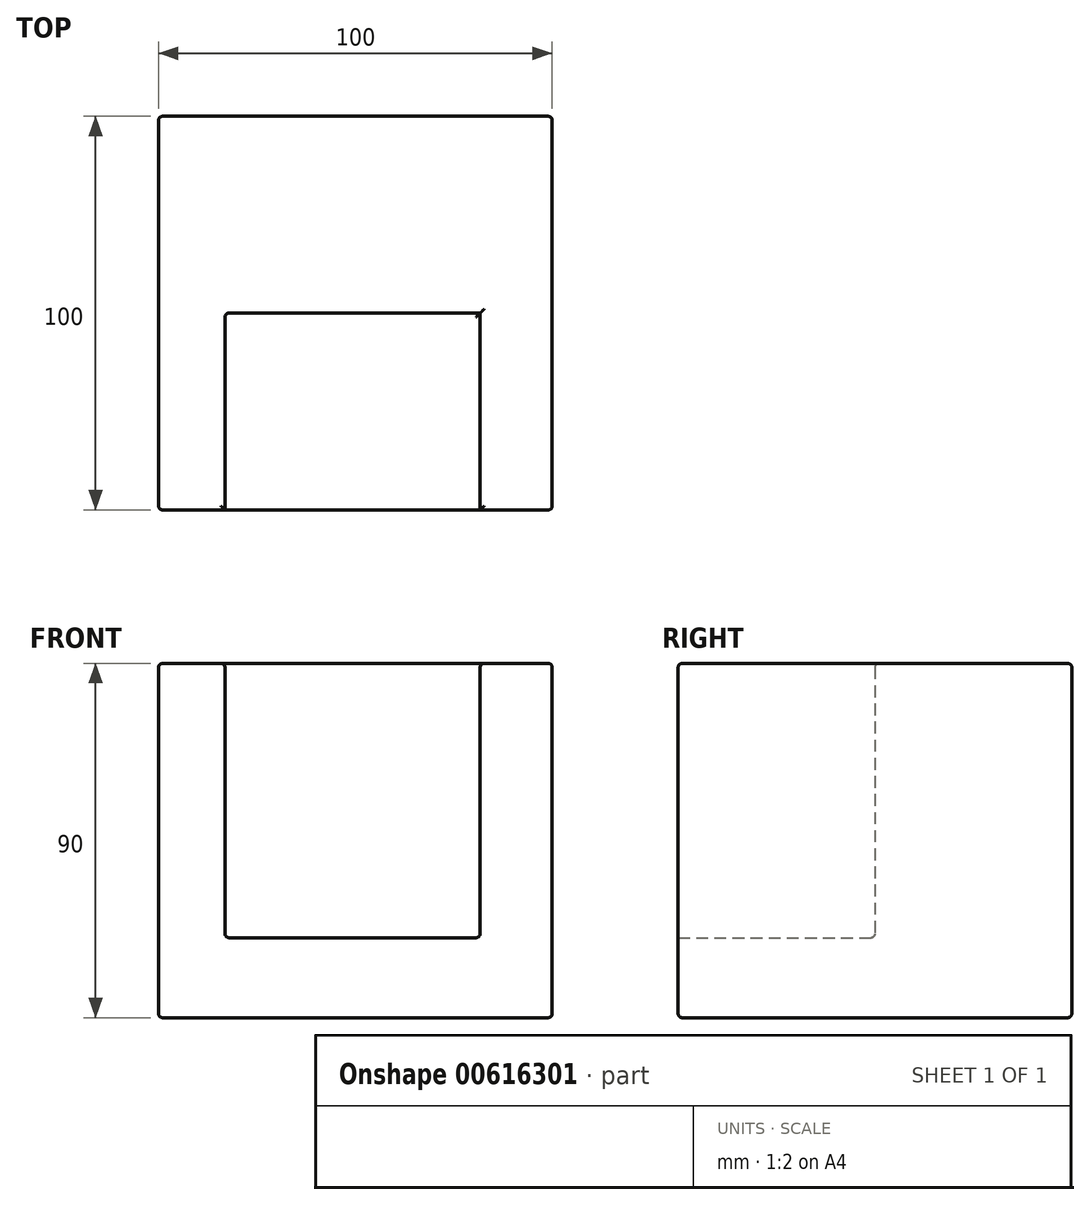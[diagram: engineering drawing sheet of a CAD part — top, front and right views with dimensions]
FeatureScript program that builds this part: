
annotation { "Feature Type Name" : "Feature", "Feature Type Description" : "" }
export const myFeature = defineFeature(function(context is Context, id is Id, definition is map)
    precondition{}
    {
        {
            var Q0;
            Q0=qCreatedBy(makeId("Top.planeOp"),FACE);
            var sketch = newSketch(context, id + "F0", { "sketchPlane" : qUnion([Q0])});
            skLineSegment(sketch, "E0.bottom", {"start": v(50, -50) * mm, "end": v(-50, -50) * mm});
            skLineSegment(sketch, "E0.top", {"start": v(50, 50) * mm, "end": v(-50, 50) * mm});
            skLineSegment(sketch, "E0.left", {"start": v(50, -50) * mm, "end": v(50, 50) * mm});
            skLineSegment(sketch, "E0.right", {"start": v(-50, -50) * mm, "end": v(-50, 50) * mm});
            skPoint(sketch, "E0.middle", {"position": v(0, 0) * mm});
            skSolve(sketch);
        }
        {
            var Q0;
            Q0 = qSketchRegion(id + "F0", true);
            extrude(context, id + "F1", {"entities" : qUnion([Q0]), "depth" : 90 * mm, "offsetDistance" : 25 * mm});
        }
        {
            var Q0;
            Q0=qCreatedBy(makeId("Front.planeOp"),FACE);
            var sketch = newSketch(context, id + "F2", { "sketchPlane" : qUnion([Q0])});
            skLineSegment(sketch, "E1.bottom", {"start": v(-33.14, 90.96) * mm, "end": v(31.7, 90.96) * mm});
            skLineSegment(sketch, "E1.top", {"start": v(-33.14, 20.32) * mm, "end": v(31.7, 20.32) * mm});
            skLineSegment(sketch, "E1.left", {"start": v(-33.14, 90.96) * mm, "end": v(-33.14, 20.32) * mm});
            skLineSegment(sketch, "E1.right", {"start": v(31.7, 90.96) * mm, "end": v(31.7, 20.32) * mm});
            skSolve(sketch);
        }
        {
            var Q0;
            Q0 = qSketchRegion(id + "F2", true);
            extrude(context, id + "F3", {"entities" : qUnion([Q0]), "operationType" : NewBodyOperationType.REMOVE, "depth" : 50 * mm, "offsetDistance" : 25 * mm});
        }
        {
            var Q0;
            Q0=qCreatedBy(makeId("Top.planeOp"),FACE);
            var sketch = newSketch(context, id + "F4", { "sketchPlane" : qUnion([Q0])});
            skLineSegment(sketch, "E2.bottom", {"start": v(-32.9, 0) * mm, "end": v(32.4, 0) * mm});
            skLineSegment(sketch, "E2.top", {"start": v(-32.9, 31.19) * mm, "end": v(32.4, 31.19) * mm});
            skLineSegment(sketch, "E2.left", {"start": v(-32.9, 0) * mm, "end": v(-32.9, 31.19) * mm});
            skLineSegment(sketch, "E2.right", {"start": v(32.4, 0) * mm, "end": v(32.4, 31.19) * mm});
            skSolve(sketch);
        }
        {
            var Q0;
            Q0 = qSketchRegion(id + "F4", true);
            extrude(context, id + "F5", {"entities" : qUnion([Q0]), "operationType" : NewBodyOperationType.ADD, "depth" : 25 * mm, "offsetDistance" : 25 * mm});
        }
        {
            var Q0;
            Q0 = qSketchRegion(id + "F4", true);
            extrude(context, id + "F6", {"entities" : qUnion([Q0]), "operationType" : NewBodyOperationType.ADD, "depth" : 50 * mm, "offsetDistance" : 25 * mm});
        }
        {
            var Q0;
            Q0=makeQuery(id+"F3.boolean.opBoolean","INTERSECT",EDGE,{"derivedFrom":[makeQuery(id+"F1.opExtrude","CAP_FACE",FACE,{"disambiguationData":[OSD([sQuery(id+"F0.wireOp",EDGE,"E0.bottom"),sQuery(id+"F0.wireOp",EDGE,"E0.top"),sQuery(id+"F0.wireOp",EDGE,"E0.left"),sQuery(id+"F0.wireOp",EDGE,"E0.right")])],"isStart":false}),makeQuery(id+"F3.opExtrude","CAP_FACE",FACE,{"disambiguationData":[OSD([sQuery(id+"F2.wireOp",EDGE,"E1.bottom"),sQuery(id+"F2.wireOp",EDGE,"E1.top"),sQuery(id+"F2.wireOp",EDGE,"E1.left"),sQuery(id+"F2.wireOp",EDGE,"E1.right")])],"isStart":true})]});
            fillet(context, id + "F7", {"entities" : qUnion([Q0]), "radius" : 1 * mm, "tangentPropagation" : true, "allowEdgeOverflow" : false});
        }
        {
            var Q0;
            Q0=makeQuery(id+"F3.boolean.opBoolean","INTERSECT",EDGE,{"derivedFrom":[makeQuery(id+"F1.opExtrude","CAP_FACE",FACE,{"disambiguationData":[OSD([sQuery(id+"F0.wireOp",EDGE,"E0.bottom"),sQuery(id+"F0.wireOp",EDGE,"E0.top"),sQuery(id+"F0.wireOp",EDGE,"E0.left"),sQuery(id+"F0.wireOp",EDGE,"E0.right")])],"isStart":false}),makeQuery(id+"F3.opExtrude","SWEPT_FACE",FACE,{"disambiguationData":[OSD([sQuery(id+"F2.wireOp",EDGE,"E1.left")])]})]});
            var Q1;
            Q1=makeQuery(id+"F3.boolean.opBoolean","INTERSECT",EDGE,{"derivedFrom":[makeQuery(id+"F1.opExtrude","CAP_FACE",FACE,{"disambiguationData":[OSD([sQuery(id+"F0.wireOp",EDGE,"E0.bottom"),sQuery(id+"F0.wireOp",EDGE,"E0.top"),sQuery(id+"F0.wireOp",EDGE,"E0.left"),sQuery(id+"F0.wireOp",EDGE,"E0.right")])],"isStart":false}),makeQuery(id+"F3.opExtrude","SWEPT_FACE",FACE,{"disambiguationData":[OSD([sQuery(id+"F2.wireOp",EDGE,"E1.right")])]})]});
            var Q2;
            {var subQ0=sQuery(id+"F0.wireOp",EDGE,"E0.bottom");var subQ1=sQuery(id+"F0.wireOp",EDGE,"E0.left");Q2=makeQuery(id+"F3.boolean.opBoolean","SPLIT",EDGE,{"disambiguationData":[TD([makeQuery(id+"F1.opExtrude","SWEPT_FACE",FACE,{"disambiguationData":[OSD([subQ1])]})])],"derivedFrom":makeQuery(id+"F1.opExtrude","CAP_EDGE",EDGE,{"disambiguationData":[OSD([subQ0])],"isStart":false})});}
            var Q3;
            Q3=makeQuery(id+"F1.opExtrude","CAP_EDGE",EDGE,{"disambiguationData":[OSD([sQuery(id+"F0.wireOp",EDGE,"E0.left")])],"isStart":false});
            var Q4;
            Q4=makeQuery(id+"F1.opExtrude","CAP_EDGE",EDGE,{"disambiguationData":[OSD([sQuery(id+"F0.wireOp",EDGE,"E0.top")])],"isStart":false});
            var Q5;
            Q5=makeQuery(id+"F1.opExtrude","CAP_EDGE",EDGE,{"disambiguationData":[OSD([sQuery(id+"F0.wireOp",EDGE,"E0.right")])],"isStart":false});
            var Q6;
            Q6=makeQuery(id+"F1.opExtrude","SWEPT_EDGE",EDGE,{"disambiguationData":[OSD([sQuery(id+"F0.wireOp",EDGE,"E0.top"),sQuery(id+"F0.wireOp",EDGE,"E0.right")])]});
            var Q7;
            Q7=makeQuery(id+"F1.opExtrude","CAP_EDGE",EDGE,{"disambiguationData":[OSD([sQuery(id+"F0.wireOp",EDGE,"E0.right")])],"isStart":true});
            var Q8;
            {var subQ0=sQuery(id+"F0.wireOp",EDGE,"E0.bottom");var subQ1=sQuery(id+"F0.wireOp",EDGE,"E0.right");Q8=makeQuery(id+"F3.boolean.opBoolean","SPLIT",EDGE,{"disambiguationData":[TD([makeQuery(id+"F1.opExtrude","SWEPT_FACE",FACE,{"disambiguationData":[OSD([subQ1])]})])],"derivedFrom":makeQuery(id+"F1.opExtrude","CAP_EDGE",EDGE,{"disambiguationData":[OSD([subQ0])],"isStart":false})});}
            var Q9;
            Q9=makeQuery(id+"F3.boolean.opBoolean","COPY",EDGE,{"derivedFrom":makeQuery(id+"F3.opExtrude","CAP_EDGE",EDGE,{"disambiguationData":[OSD([sQuery(id+"F2.wireOp",EDGE,"E1.left")])],"isStart":false})});
            var Q10;
            Q10=makeQuery(id+"F1.opExtrude","CAP_EDGE",EDGE,{"disambiguationData":[OSD([sQuery(id+"F0.wireOp",EDGE,"E0.bottom")])],"isStart":true});
            var Q11;
            Q11=makeQuery(id+"F3.boolean.opBoolean","COPY",EDGE,{"derivedFrom":makeQuery(id+"F3.opExtrude","CAP_EDGE",EDGE,{"disambiguationData":[OSD([sQuery(id+"F2.wireOp",EDGE,"E1.top")])],"isStart":false})});
            var Q12;
            Q12=makeQuery(id+"F3.boolean.opBoolean","COPY",EDGE,{"derivedFrom":makeQuery(id+"F3.opExtrude","SWEPT_EDGE",EDGE,{"disambiguationData":[OSD([sQuery(id+"F2.wireOp",EDGE,"E1.top"),sQuery(id+"F2.wireOp",EDGE,"E1.right")])]})});
            var Q13;
            Q13=makeQuery(id+"F3.boolean.opBoolean","COPY",EDGE,{"derivedFrom":makeQuery(id+"F3.opExtrude","CAP_EDGE",EDGE,{"disambiguationData":[OSD([sQuery(id+"F2.wireOp",EDGE,"E1.right")])],"isStart":false})});
            var Q14;
            Q14=makeQuery(id+"F1.opExtrude","SWEPT_EDGE",EDGE,{"disambiguationData":[OSD([sQuery(id+"F0.wireOp",EDGE,"E0.bottom"),sQuery(id+"F0.wireOp",EDGE,"E0.left")])]});
            var Q15;
            Q15=makeQuery(id+"F3.boolean.opBoolean","COPY",EDGE,{"derivedFrom":makeQuery(id+"F3.opExtrude","CAP_EDGE",EDGE,{"disambiguationData":[OSD([sQuery(id+"F2.wireOp",EDGE,"E1.top")])],"isStart":true})});
            var Q16;
            Q16=makeQuery(id+"F3.boolean.opBoolean","COPY",EDGE,{"derivedFrom":makeQuery(id+"F3.opExtrude","SWEPT_EDGE",EDGE,{"disambiguationData":[OSD([sQuery(id+"F2.wireOp",EDGE,"E1.top"),sQuery(id+"F2.wireOp",EDGE,"E1.left")])]})});
            var Q17;
            Q17=makeQuery(id+"F3.boolean.opBoolean","COPY",EDGE,{"derivedFrom":makeQuery(id+"F3.opExtrude","CAP_EDGE",EDGE,{"disambiguationData":[OSD([sQuery(id+"F2.wireOp",EDGE,"E1.left")])],"isStart":true})});
            var Q18;
            Q18=makeQuery(id+"F1.opExtrude","SWEPT_EDGE",EDGE,{"disambiguationData":[OSD([sQuery(id+"F0.wireOp",EDGE,"E0.bottom"),sQuery(id+"F0.wireOp",EDGE,"E0.right")])]});
            var Q19;
            Q19=makeQuery(id+"F1.opExtrude","SWEPT_EDGE",EDGE,{"disambiguationData":[OSD([sQuery(id+"F0.wireOp",EDGE,"E0.top"),sQuery(id+"F0.wireOp",EDGE,"E0.left")])]});
            var Q20;
            Q20=makeQuery(id+"F1.opExtrude","CAP_EDGE",EDGE,{"disambiguationData":[OSD([sQuery(id+"F0.wireOp",EDGE,"E0.left")])],"isStart":true});
            var Q21;
            Q21=makeQuery(id+"F1.opExtrude","CAP_EDGE",EDGE,{"disambiguationData":[OSD([sQuery(id+"F0.wireOp",EDGE,"E0.top")])],"isStart":true});
            fillet(context, id + "F8", {"entities" : qUnion([Q0, Q1, Q2, Q3, Q4, Q5, Q6, Q7, Q8, Q9, Q10, Q11, Q12, Q13, Q14, Q15, Q16, Q17, Q18, Q19, Q20, Q21]), "radius" : 1 * mm, "tangentPropagation" : true, "allowEdgeOverflow" : false});
        }
    });
